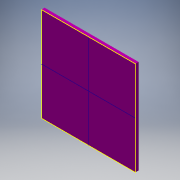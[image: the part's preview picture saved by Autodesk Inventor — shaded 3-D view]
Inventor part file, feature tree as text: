
AUTODESK INVENTOR PART (.ipt)
format: ipt  version: 2016 (Build 200138000, 138)  size: 91,136 bytes
history: native  units: mm
features: sketch x2, extrude x1
ambient origin geometry x8: Origin, YZ Plane, XZ Plane, XY Plane, X Axis, Y Axis, Z Axis, Center Point
bodies: Solid1 (feature_tree)
feature tree (3):
  extrude  "Extrusion1"  Depth=50.0mm
  sketch  "Sketch2"  dims[d2=1.7mm d3=0.0mm]
  sketch  "Sketch1"  dims[d0=50.0mm d1=50.0mm]
